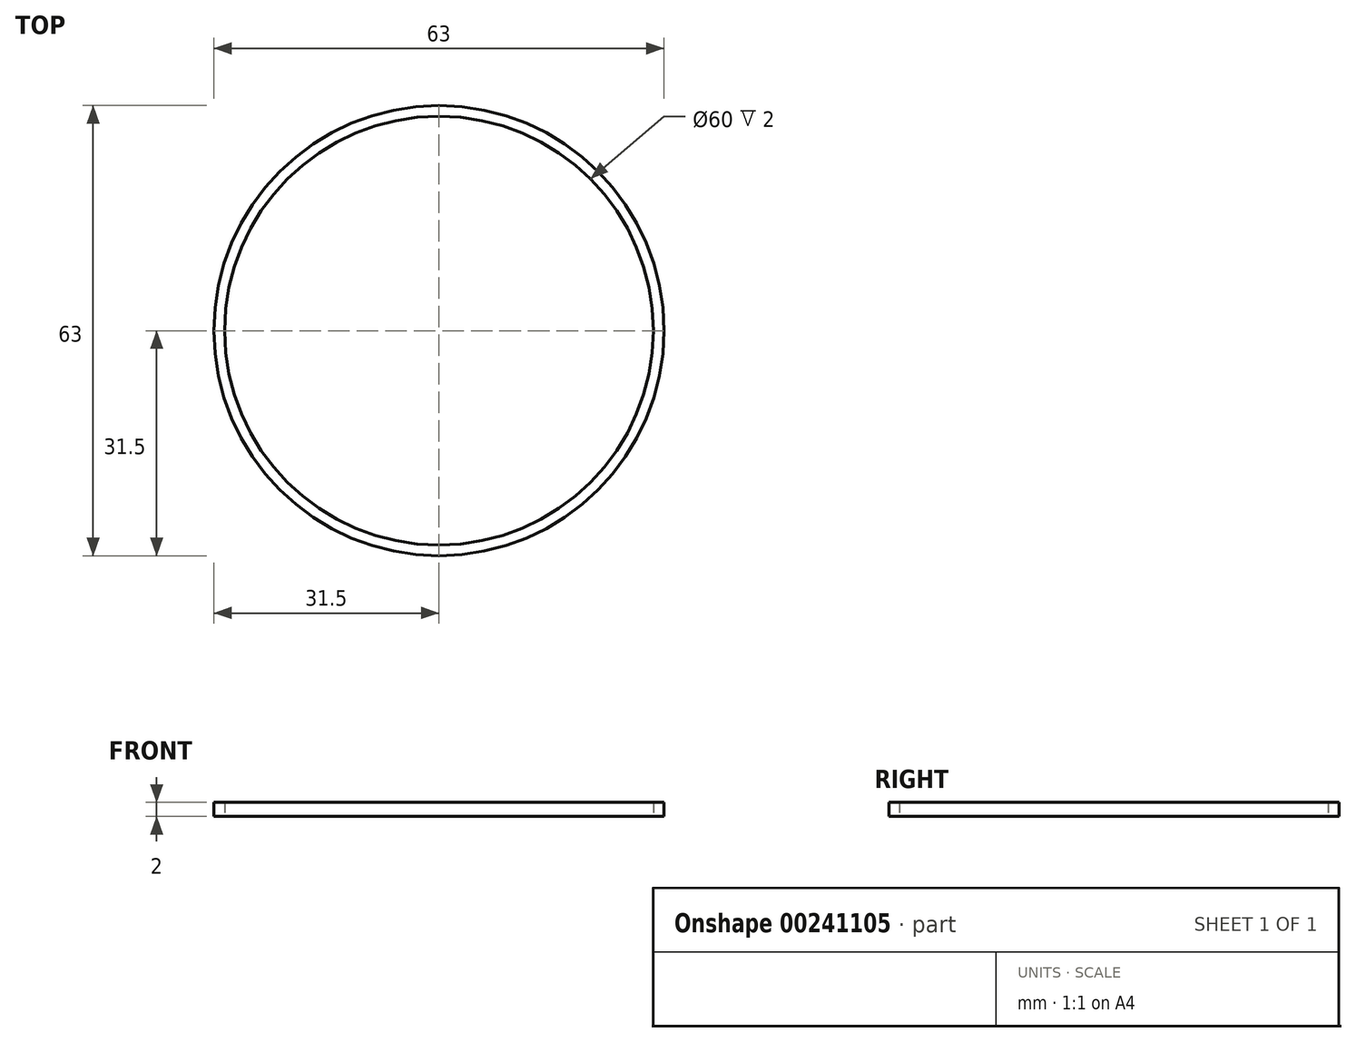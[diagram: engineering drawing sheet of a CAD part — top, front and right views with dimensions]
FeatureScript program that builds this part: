
annotation { "Feature Type Name" : "Feature", "Feature Type Description" : "" }
export const myFeature = defineFeature(function(context is Context, id is Id, definition is map)
    precondition{}
    {
        {
            var Q0;
            Q0=qCreatedBy(makeId("Top.planeOp"),FACE);
            var sketch = newSketch(context, id + "F0", { "sketchPlane" : qUnion([Q0])});
            skPoint(sketch, "E0.center", {"position": v(0, 0) * mm});
            skCircle(sketch, "E1", {"center": v(0, 0) * mm, "radius": 31.5 * mm});
            skCircle(sketch, "E2", {"center": v(0, 0) * mm, "radius": 30 * mm});
            skSolve(sketch);
        }
        {
            var Q0;
            Q0=qSketchRegion(id+"F0",true);
            extrude(context, id + "F1", {"entities" : qUnion([Q0]), "depth" : 2 * mm});
        }
    });
